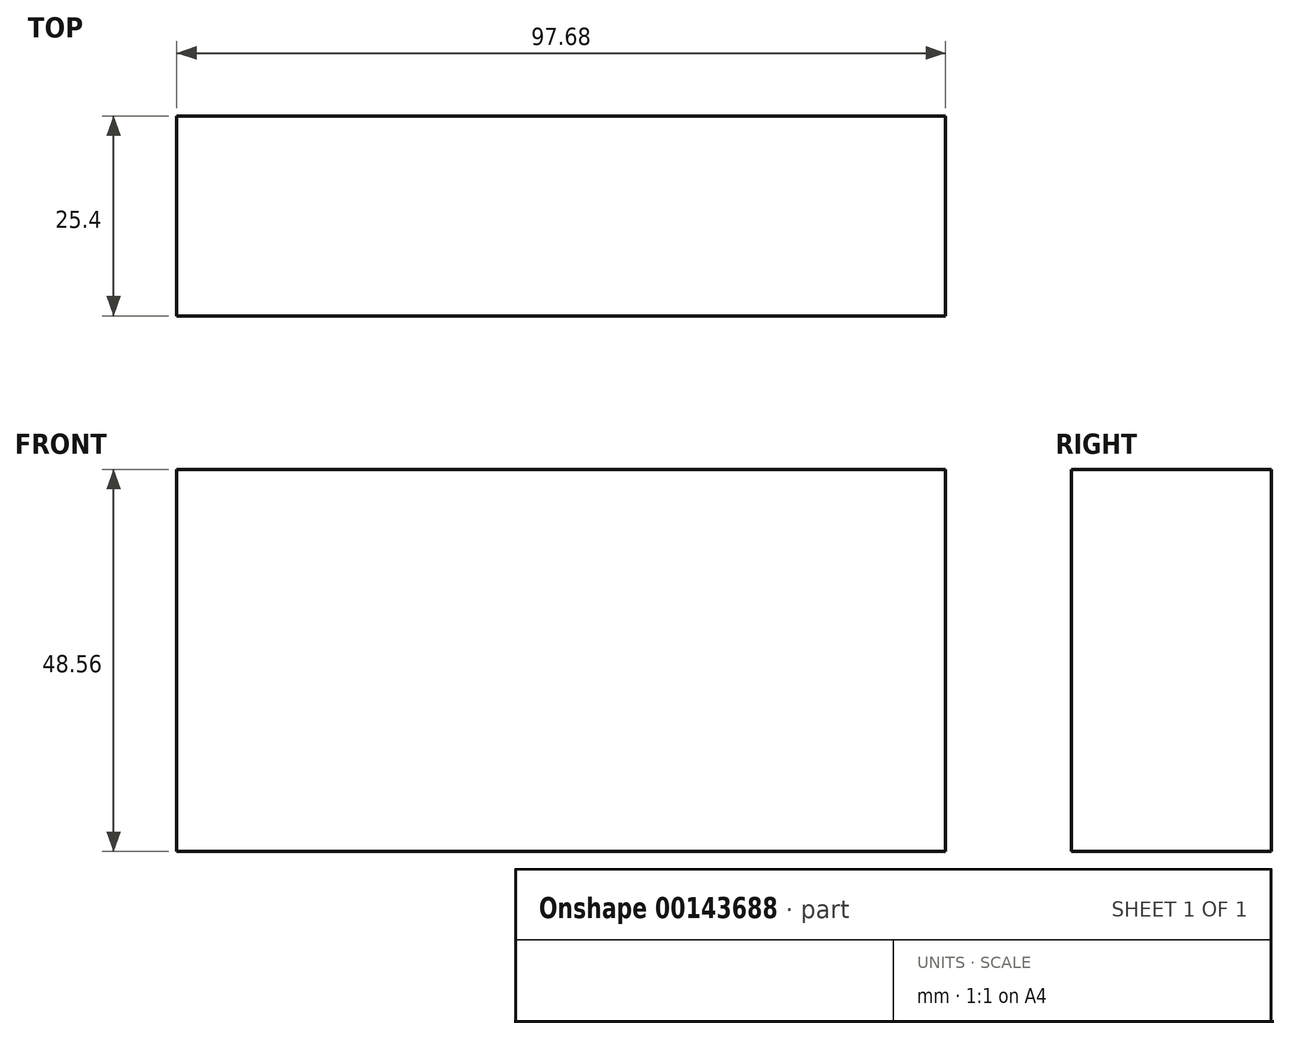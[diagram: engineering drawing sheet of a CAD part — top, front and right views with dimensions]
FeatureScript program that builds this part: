
annotation { "Feature Type Name" : "Feature", "Feature Type Description" : "" }
export const myFeature = defineFeature(function(context is Context, id is Id, definition is map)
    precondition{}
    {
        {
            var Q0;
            Q0=qCreatedBy(makeId("Front.planeOp"),FACE);
            var sketch = newSketch(context, id + "F0", { "sketchPlane" : qUnion([Q0])});
            skLineSegment(sketch, "E0.bottom", {"start": v(-48.84, 24.28) * mm, "end": v(48.84, 24.28) * mm});
            skLineSegment(sketch, "E0.top", {"start": v(-48.84, -24.28) * mm, "end": v(48.84, -24.28) * mm});
            skLineSegment(sketch, "E0.left", {"start": v(-48.84, 24.28) * mm, "end": v(-48.84, -24.28) * mm});
            skLineSegment(sketch, "E0.right", {"start": v(48.84, 24.28) * mm, "end": v(48.84, -24.28) * mm});
            skPoint(sketch, "E0.middle", {"position": v(0, 0) * mm});
            skSolve(sketch);
        }
        {
            var Q0;
            Q0=qSketchRegion(id+"F0",true);
            extrude(context, id + "F1", {"entities" : qUnion([Q0]), "depth" : 25.4 * mm});
        }
    });
